# Revit family: 57122209
name_source: partatom
category: Plumbing Fixtures
revit_build: Autodesk Revit 2017 (Build: 20190508_0315(x64)
units: mm (PartAtom-declared; Revit-internal decimal feet)

## family parameters
Always vertical = Yes
Cut with Voids When Loaded = No
OmniClass Number = 23.45.55.00
OmniClass Title = Sanitary Faucets, Wastes
Part Type = Normal
Room Calculation Point = No
Round Connector Dimension = Use Diameter
Shared = No
Work Plane-Based = No

## types (1)
- 57122209 Washbasin faucet, 9/12 V, Bluetooth
    2D/3D/BIM Files URL = http://static.hansa.com
    Advanced Features = Adjustable settings (via bluetooth)
    Aerator = HONEYCOMB®
    Afterflow Period = 3.0 s
    AssetType = Fixed
    Automatic Flush = off (off/1-120 h)
    Automatic Flush Period = 30 s (1-1800 s)
    BIMObjectName = 57122209
    Backflow Prevention EN1717 = AA
    Bluetooth = 4.x
    BodyMaterial = Brass
    Brand = Hansa
    Catalog Drawing URL = http://static.hansa.com
    Category = Bathroom;Public & Semi-public
    Class = Touchless;Bluetooth®;Plug transformer
    CloseOffRating = 0
    Color = Chrome
    Connection = Flexible Inlet Pipes
    Connection Size = G3/8
    Constituents = Single lever
    ConvergoRefNr = 0087-2003-0039-FI
    Customs Code = 84818011
    DN Size = DN15
    Dimension Drawing URL = http://static.hansa.com
    DurationUnit = Year
    EAN Number = 4057304014062
    EMC Directive = 2014/30/EU
    EN Standard = EN 15091
    Electrical Connection = 9 / 12 V
    Electronic Parts = Autofocus sensor;Solenoid valve
    Extensions = Rapid pop-up waste
    FDV Document URL = http://www.hansa.com
    FaucetMainMaterial = Brass
    Features = Touchless;Bluetooth®;Plug transformer
    Finish = Polished
    Flow Drawing URL = http://static.hansa.com
    Flow Rate At 300kPa With Flow Controller = 0.1 L/s
    FlowCoefficient = 0
    Group = Washbasin Faucets
    IfcExportAs = IfcValveType
    IfcExportType = FAUCET
    InletConnectionSize = 10 mm  [stored 0.0328084 ft]
    Installation Type = Deck mounted
    Installation and Maintenance = http://static.hansa.com
    Lever Handle = Temperature control handle
    ManufacterURL = http://www.hansa.com
    Manufacturer = Hansa
    ManufacturerName = Hansa
    Market = AUT;BEL;CZE;DEU;ESP;FRA;INT;ITA;NLD;SVK
    Material = Brass
    Max Flow Period = 120.0 s
    Max. Hot Water Supply = 70 °C
    Mechanical Parts = Litter filter(s);Mixing valve;Non-return valve(s)
    Model = 57122209 Washbasin faucet, 9/12 V, Bluetooth
    ModelReference = 57122209
    Mounting Holes = 1 Mounting Hole
    NBSDescription = Water supply fittings for baths
    NBSReference = 45-35-70/315
    Name = 57122209 Washbasin faucet, 9/12 V, Bluetooth
    Name_en = 57122209 Washbasin faucet, 9/12 V, Bluetooth
    NominalDepth = 168 mm
    NominalHeight = 130 mm
    NominalWidth = 66 mm
    Operating Voltage = 12 V
    Package Weight = 2.028 kg
    Package external Dimensions = 290 x 210 x 90
    Product Code = 57122209
    Product Datasheet = http://www.hansa.com
    Product Family = HANSASTELA
    Product Image URL = http://static.hansa.com
    Product URL = http://static.hansa.com
    Projection = 126 mm  [stored 0.413386 ft]
    Protection Class = IP 55
    Shape = Sculptured
    Size = 65x170x130 mm
    Spare Parts = http://static.hansa.com
    Spout Type = Fixed spout
    Temperature = Temperature limiter (retrofittable)
    Uniclass2 = Pr_40_30_96_78
    Uniclass2015Description = Shower manual water supply sets
    Uniclass2015Reference = Pr_40_20_87_78
    Version = 1
    VersionDate = 06/04/2020
    WarrantyDescription = http://warranty.hansa.com
    WarrantyDurationUnit = Year
    WorkingPressure = 50 - 1000 kPa

note: [stored X ft] marks values corroborated as IEEE doubles in the binary element streams (Revit-internal decimal feet)

## geometry (parser evidence)
native form markers: Sweep x6
no freeform markers — native parametric forms only
